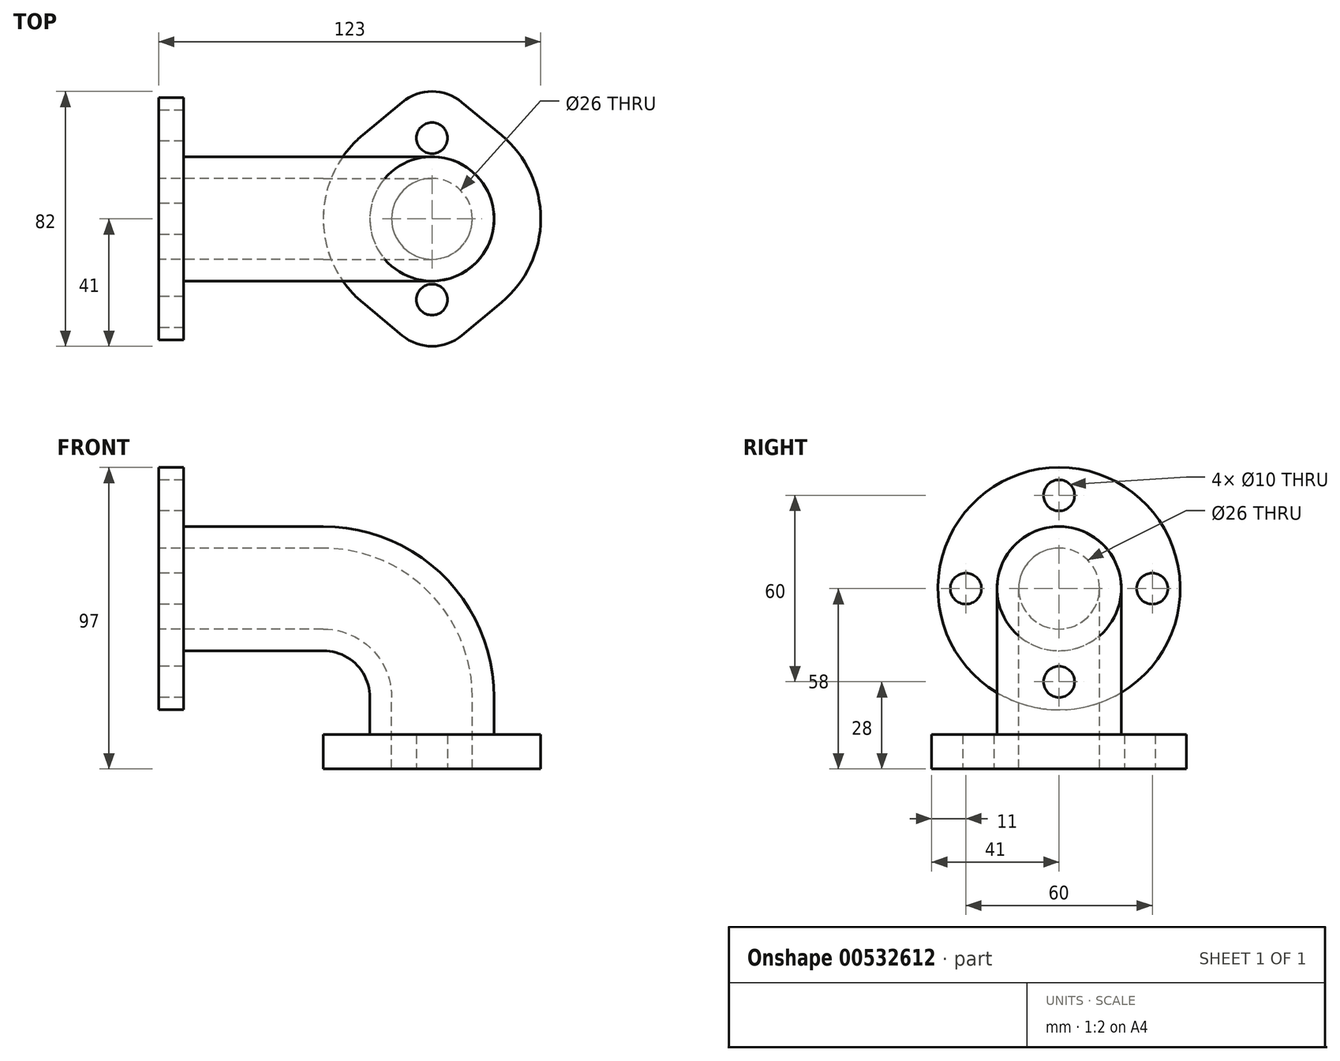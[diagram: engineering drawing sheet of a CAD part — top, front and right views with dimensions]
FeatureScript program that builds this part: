
annotation { "Feature Type Name" : "Feature", "Feature Type Description" : "" }
export const myFeature = defineFeature(function(context is Context, id is Id, definition is map)
    precondition{}
    {
        {
            var Q0;
            Q0=qCreatedBy(makeId("Top.planeOp"),FACE);
            var sketch = newSketch(context, id + "F0", { "sketchPlane" : qUnion([Q0])});
            skCircle(sketch, "E0", {"center": v(0, 0) * mm, "radius": 13 * mm});
            skCircle(sketch, "E1", {"center": v(0, 0) * mm, "radius": 20 * mm});
            skSolve(sketch);
        }
        {
            var Q0;
            Q0=qCreatedBy(makeId("Front.planeOp"),FACE);
            var sketch = newSketch(context, id + "F1", { "sketchPlane" : qUnion([Q0])});
            skLineSegment(sketch, "E2", {"start": v(0, 0) * mm, "end": v(0, 23) * mm});
            skLineSegment(sketch, "E3", {"start": v(-35, 58) * mm, "end": v(-88, 58) * mm});
            skPoint(sketch, "E4.visualSharp", {"position": v(0, 58) * mm});
            skArc(sketch, "E4.filletArc", {"start": v(0, 23) * mm, "mid": v(-10.25, 47.75) * mm, "end": v(-35, 58) * mm});
            skSolve(sketch);
        }
        {
            var Q0;
            Q0=makeQuery(id+"F0.imprint","IMPRINT",FACE,{"disambiguationData":[TD([[makeQuery(id+"F0.imprint","IMPRINT",EDGE,{"derivedFrom":sQuery(id+"F0.wireOp",EDGE,"E0")}),-1.0]])]});
            var Q1;
            Q1 = qConstructionFilter(qBodyType(qCreatedBy(id + "F1" ,EDGE), BodyType.WIRE), ConstructionObject.NO);
            sweep(context, id + "F2", {"profiles" : qUnion([Q0]), "path" : qUnion([Q1])});
        }
        {
            var Q0;
            Q0=makeQuery(id+"F2.opSweep","CAP_FACE",FACE,{"disambiguationData":[OSD([sQuery(id+"F0.wireOp",EDGE,"E0"),sQuery(id+"F0.wireOp",EDGE,"E1"),sQuery(id+"F1.wireOp",VERTEX,"E3.end")])],"isStart":false});
            var sketch = newSketch(context, id + "F3", { "sketchPlane" : qUnion([Q0])});
            skCircle(sketch, "E5", {"center": v(0, 58) * mm, "radius": 39 * mm});
            skCircle(sketch, "E6", {"center": v(0, 58) * mm, "radius": 30 * mm});
            skCircle(sketch, "E7", {"center": v(30, 58) * mm, "radius": 5 * mm});
            skCircle(sketch, "E8.1.0", {"center": v(0, 88) * mm, "radius": 5 * mm});
            skCircle(sketch, "E8.2.0", {"center": v(-30, 58) * mm, "radius": 5 * mm});
            skCircle(sketch, "E8.3.0", {"center": v(0, 28) * mm, "radius": 5 * mm});
            skSolve(sketch);
        }
        {
            var Q0;
            {var subQ0=sQuery(id+"F1.wireOp",VERTEX,"E3.end");Q0=makeQuery(id+"F3.imprint","IMPRINT",FACE,{"disambiguationData":[TD([[makeQuery(id+"F3.imprint","IMPRINT",EDGE,{"derivedFrom":makeQuery(id+"F2.opSweep","CAP_EDGE",EDGE,{"disambiguationData":[OSD([sQuery(id+"F0.wireOp",EDGE,"E0"),subQ0])],"isStart":false})}),-1.0]])]});}
            var Q1;
            Q1=makeQuery(id+"F3.imprint","IMPRINT",FACE,{"disambiguationData":[TD([[makeQuery(id+"F3.imprint","IMPRINT",EDGE,{"derivedFrom":makeQuery(id+"F2.opSweep","CAP_EDGE",EDGE,{"disambiguationData":[OSD([sQuery(id+"F0.wireOp",EDGE,"E1"),sQuery(id+"F1.wireOp",VERTEX,"E3.end")])],"isStart":false})}),-1.0]])]});
            var Q2;
            Q2=makeQuery(id+"F3.imprint","IMPRINT",FACE,{"disambiguationData":[TD([[makeQuery(id+"F3.imprint","IMPRINT",EDGE,{"derivedFrom":sQuery(id+"F3.wireOp",EDGE,"E5")}),1.0]])]});
            extrude(context, id + "F4", {"entities" : qUnion([Q0, Q1, Q2]), "operationType" : NewBodyOperationType.ADD, "oppositeDirection" : true, "depth" : 8 * mm, "offsetDistance" : 25 * mm});
        }
        {
            var Q0;
            Q0=qCreatedBy(makeId("Top.planeOp"),FACE);
            var sketch = newSketch(context, id + "F5", { "sketchPlane" : qUnion([Q0])});
            skCircle(sketch, "E9", {"center": v(0, 26) * mm, "radius": 5 * mm});
            skCircle(sketch, "E10", {"center": v(0, -26) * mm, "radius": 5 * mm});
            skArc(sketch, "E11", {"start": v(9.58, 37.54) * mm, "mid": v(0, 41) * mm, "end": v(-9.58, 37.54) * mm});
            skArc(sketch, "E12", {"start": v(-9.58, -37.54) * mm, "mid": v(0, -41) * mm, "end": v(9.58, -37.54) * mm});
            skLineSegment(sketch, "E13", {"start": v(22.36, 26.92) * mm, "end": v(9.58, 37.54) * mm});
            skLineSegment(sketch, "E14.MirrorCS", {"start": v(22.36, -26.92) * mm, "end": v(9.58, -37.54) * mm});
            skLineSegment(sketch, "E15.MirrorCS", {"start": v(-22.36, 26.92) * mm, "end": v(-9.58, 37.54) * mm});
            skLineSegment(sketch, "E16.MirrorCS", {"start": v(-22.36, -26.92) * mm, "end": v(-9.58, -37.54) * mm});
            skArc(sketch, "E17.trimOffspring", {"start": v(-22.36, 26.92) * mm, "mid": v(-35, 0) * mm, "end": v(-22.36, -26.92) * mm});
            skArc(sketch, "E18.trimOffspring", {"start": v(22.36, -26.92) * mm, "mid": v(35, 0) * mm, "end": v(22.36, 26.92) * mm});
            skCircle(sketch, "E19.0", {"center": v(0, 0) * mm, "radius": 13 * mm});
            skSolve(sketch);
        }
        {
            var Q0;
            Q0=makeQuery(id+"F5.imprint","IMPRINT",FACE,{"disambiguationData":[TD([[makeQuery(id+"F5.imprint","IMPRINT",EDGE,{"derivedFrom":sQuery(id+"F5.wireOp",EDGE,"E9")}),-1.0]])]});
            extrude(context, id + "F6", {"entities" : qUnion([Q0]), "operationType" : NewBodyOperationType.ADD, "depth" : 11 * mm, "offsetDistance" : 25 * mm});
        }
    });
